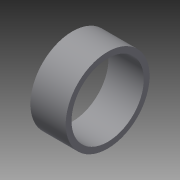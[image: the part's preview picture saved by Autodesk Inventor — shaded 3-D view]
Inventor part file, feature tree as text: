
AUTODESK INVENTOR PART (.ipt)
format: ipt  version: 2015 SP1 (Build 190203100, 203)  size: 81,920 bytes
history: native  units: in
note: dims shown in document units (in); Inventor stores cm internally (conversion verified against a paired STEP export)
features: extrude x1, sketch x1
ambient origin geometry x8: Origin, YZ Plane, XZ Plane, XY Plane, X Axis, Y Axis, Z Axis, Center Point
bodies: Solid1 (feature_tree)
feature tree (2):
  extrude  "Extrusion1"  Depth=1.0in
  sketch  "Sketch1"  dims[d0=2.047in d1=2.375in d2=1.0in d3=0.0in]
